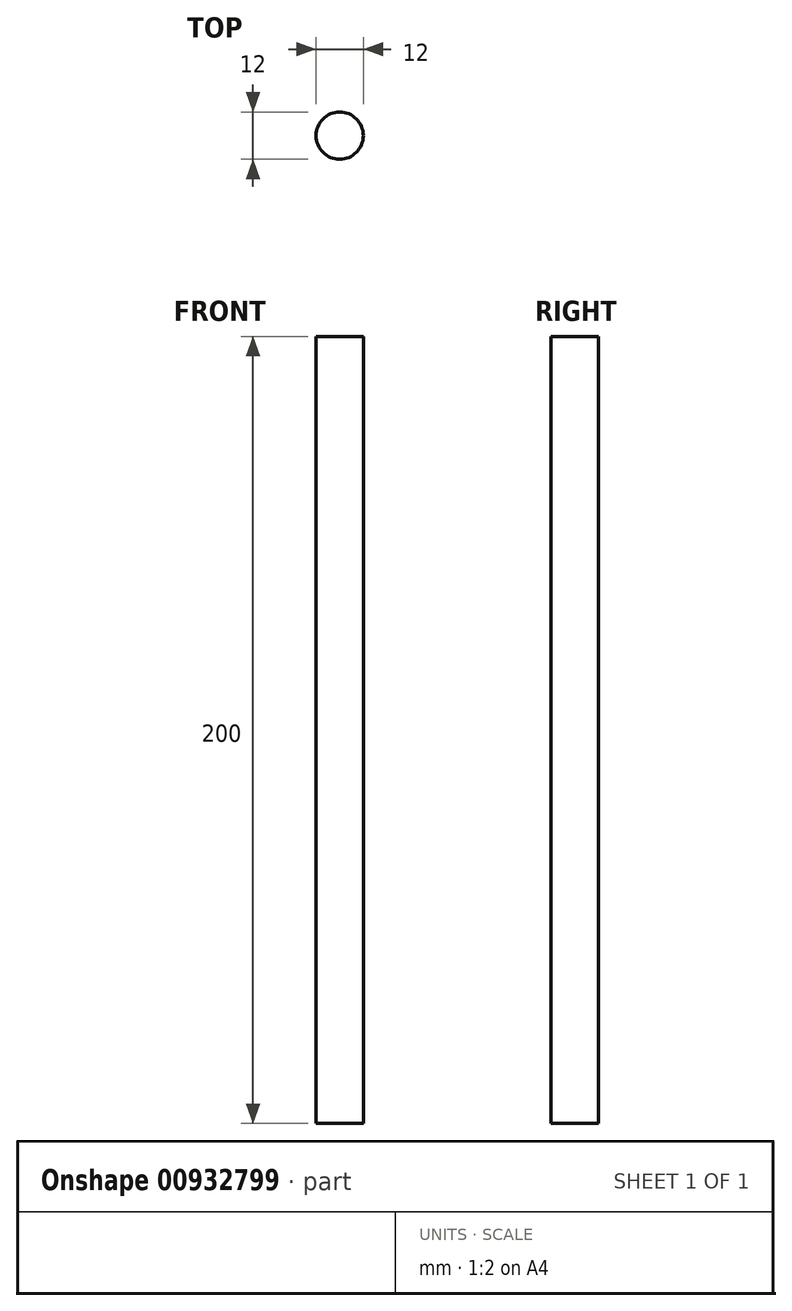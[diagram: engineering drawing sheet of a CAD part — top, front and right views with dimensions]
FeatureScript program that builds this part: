
annotation { "Feature Type Name" : "Feature", "Feature Type Description" : "" }
export const myFeature = defineFeature(function(context is Context, id is Id, definition is map)
    precondition{}
    {
        {
            var Q0;
            Q0=qCreatedBy(makeId("Top.planeOp"),FACE);
            var sketch = newSketch(context, id + "F0", { "sketchPlane" : qUnion([Q0])});
            skCircle(sketch, "E0", {"center": v(0, 0) * mm, "radius": 6 * mm});
            skSolve(sketch);
        }
        {
            var Q0;
            Q0 = qSketchRegion(id + "F0", true);
            extrude(context, id + "F1", {"entities" : qUnion([Q0]), "depth" : 200 * mm, "offsetDistance" : 25 * mm});
        }
    });
